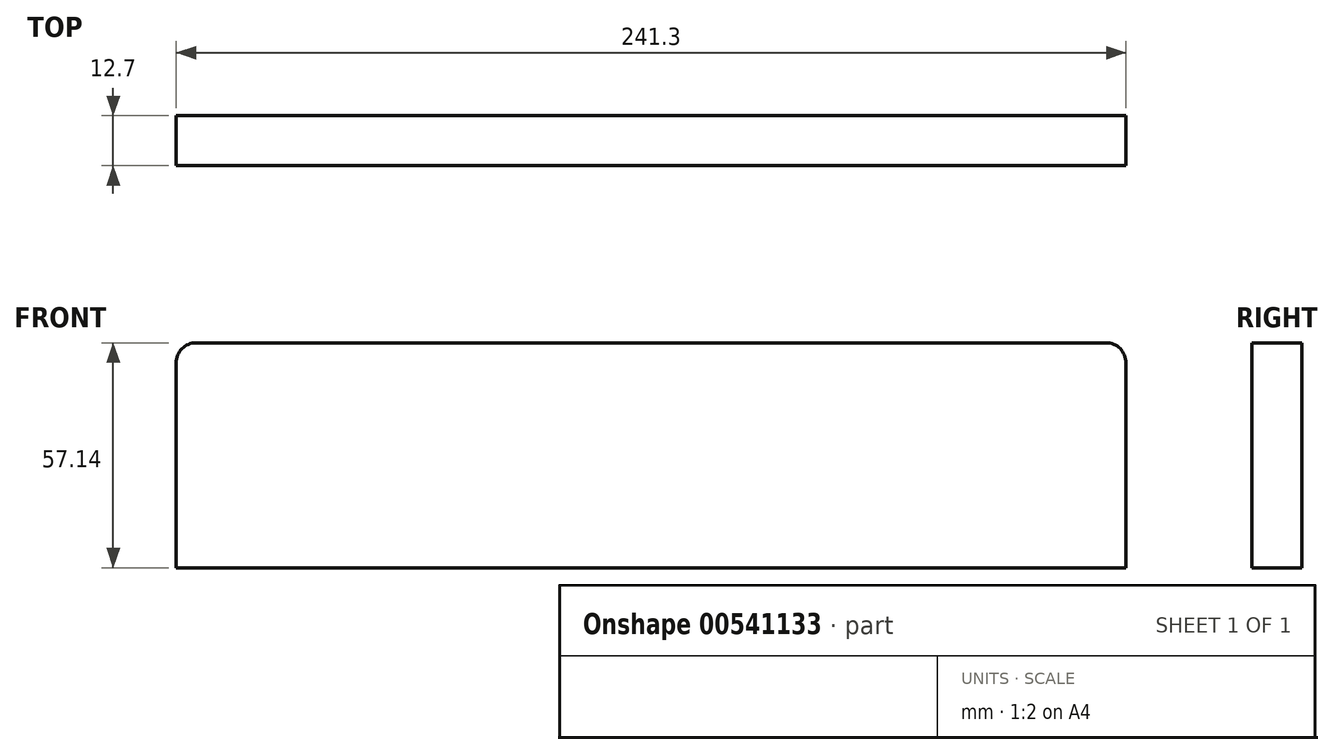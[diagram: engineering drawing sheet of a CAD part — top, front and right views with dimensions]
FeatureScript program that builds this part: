
annotation { "Feature Type Name" : "Feature", "Feature Type Description" : "" }
export const myFeature = defineFeature(function(context is Context, id is Id, definition is map)
    precondition{}
    {
        {
            var Q0;
            Q0=qCreatedBy(makeId("Front.planeOp"),FACE);
            var sketch = newSketch(context, id + "F0", { "sketchPlane" : qUnion([Q0])});
            skLineSegment(sketch, "E0.bottom", {"start": v(120.65, -28.57) * mm, "end": v(-120.65, -28.58) * mm});
            skLineSegment(sketch, "E0.top", {"start": v(120.65, 28.58) * mm, "end": v(-120.65, 28.57) * mm});
            skLineSegment(sketch, "E0.left", {"start": v(120.65, -28.57) * mm, "end": v(120.65, 28.58) * mm});
            skLineSegment(sketch, "E0.right", {"start": v(-120.65, -28.58) * mm, "end": v(-120.65, 28.57) * mm});
            skPoint(sketch, "E0.middle", {"position": v(0, 0) * mm});
            skSolve(sketch);
        }
        {
            var Q0;
            Q0 = qSketchRegion(id + "F0", true);
            extrude(context, id + "F1", {"entities" : qUnion([Q0]), "depth" : 12.7 * mm, "offsetDistance" : 25.4 * mm});
        }
        {
            var Q0;
            Q0=makeQuery(id+"F1.opExtrude","SWEPT_EDGE",EDGE,{"disambiguationData":[OSD([sQuery(id+"F0.wireOp",EDGE,"E0.top"),sQuery(id+"F0.wireOp",EDGE,"E0.right")])]});
            var Q1;
            Q1=makeQuery(id+"F1.opExtrude","SWEPT_EDGE",EDGE,{"disambiguationData":[OSD([sQuery(id+"F0.wireOp",EDGE,"E0.top"),sQuery(id+"F0.wireOp",EDGE,"E0.left")])]});
            fillet(context, id + "F2", {"entities" : qUnion([Q0, Q1]), "radius" : 5.08 * mm, "tangentPropagation" : true, "allowEdgeOverflow" : false});
        }
    });
